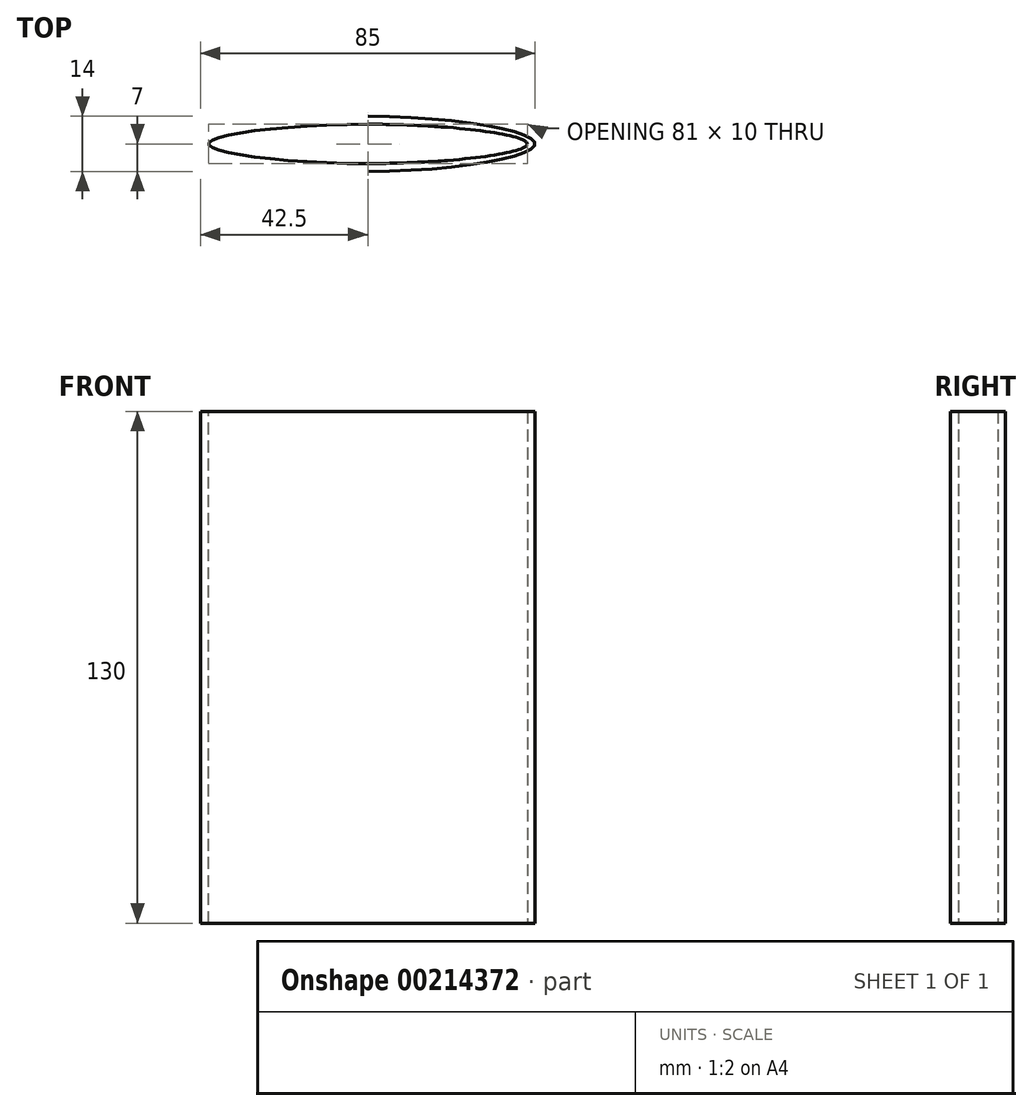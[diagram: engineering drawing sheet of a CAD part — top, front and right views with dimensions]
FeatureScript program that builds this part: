
annotation { "Feature Type Name" : "Feature", "Feature Type Description" : "" }
export const myFeature = defineFeature(function(context is Context, id is Id, definition is map)
    precondition{}
    {
        {
            var Q0;
            Q0=qCreatedBy(makeId("Top.planeOp"),FACE);
            var sketch = newSketch(context, id + "F0", { "sketchPlane" : qUnion([Q0])});
            skLineSegment(sketch, "E0", {"start": v(0, 5) * mm, "end": v(0, -5) * mm});
            skFitSpline(sketch, "E1", {"points": [v(0, 5) * mm, v(40.5, 0) * mm, v(0, -5) * mm], "startDerivative": vector(121.5, 0) * mm, "endDerivative": vector(-121.5, 0) * mm});
            skFitSpline(sketch, "E2.MirrorCS", {"points": [v(0, 5) * mm, v(-40.5, 0) * mm, v(0, -5) * mm], "startDerivative": vector(-121.5, 0) * mm, "endDerivative": vector(121.5, 0) * mm});
            skLineSegment(sketch, "E3", {"start": v(0, 0) * mm, "end": v(20.25, 0) * mm});
            skLineSegment(sketch, "E4", {"start": v(40.5, 0) * mm, "end": v(20.25, 0) * mm});
            skLineSegment(sketch, "E5", {"start": v(20.25, 5) * mm, "end": v(20.25, -5) * mm});
            skFitSpline(sketch, "E6", {"points": [v(0, 7) * mm, v(42.5, 0) * mm, v(0, -7) * mm, v(-42.5, 0) * mm, v(0, 7) * mm]});
            skLineSegment(sketch, "E7", {"start": v(0, 7) * mm, "end": v(0, -7) * mm});
            skSolve(sketch);
        }
        {
            var Q0;
            Q0 = qSketchRegion(id + "F0", true);
            extrude(context, id + "F1", {"entities" : qUnion([Q0]), "depth" : 130 * mm});
        }
    });
